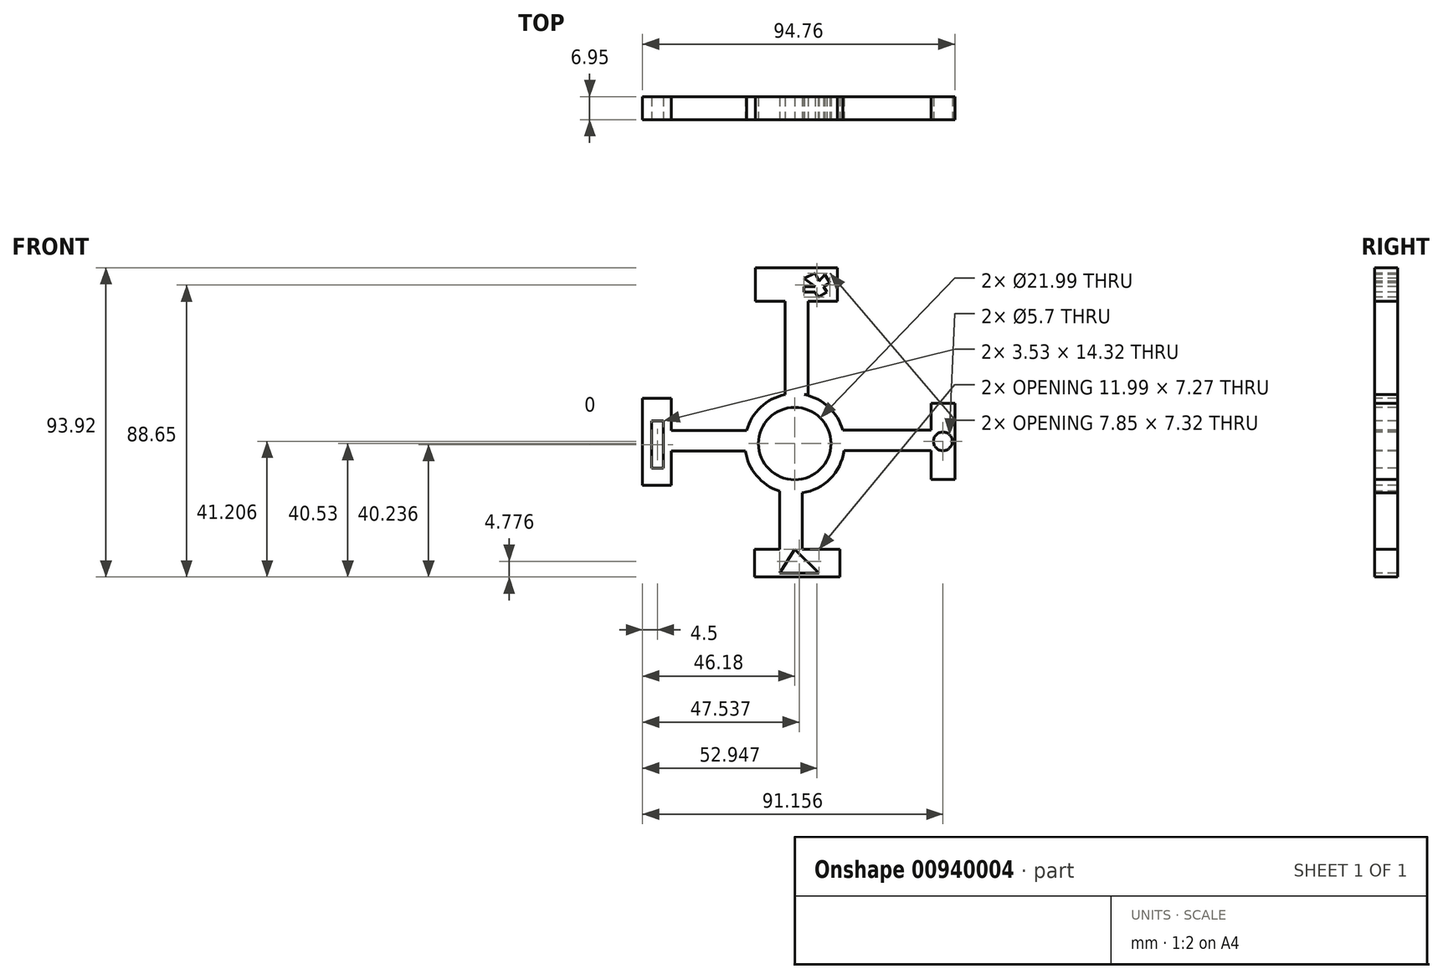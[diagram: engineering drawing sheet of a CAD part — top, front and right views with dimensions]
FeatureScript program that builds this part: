
annotation { "Feature Type Name" : "Feature", "Feature Type Description" : "" }
export const myFeature = defineFeature(function(context is Context, id is Id, definition is map)
    precondition{}
    {
        {
            var Q0;
            Q0=qCreatedBy(makeId("Front.planeOp"),FACE);
            var sketch = newSketch(context, id + "F0", { "sketchPlane" : qUnion([Q0])});
            skCircle(sketch, "E0", {"center": v(0, 0) * mm, "radius": 15.15 * mm});
            skLineSegment(sketch, "E1.bottom", {"start": v(-2.97, 14.85) * mm, "end": v(4.06, 14.85) * mm});
            skLineSegment(sketch, "E1.top", {"start": v(-2.97, 43.18) * mm, "end": v(4.06, 43.18) * mm});
            skLineSegment(sketch, "E1.left", {"start": v(-2.97, 14.85) * mm, "end": v(-2.97, 43.18) * mm});
            skLineSegment(sketch, "E1.right", {"start": v(4.06, 14.85) * mm, "end": v(4.06, 43.18) * mm});
            skLineSegment(sketch, "E2.bottom", {"start": v(-14.61, 4) * mm, "end": v(-37.47, 4) * mm});
            skLineSegment(sketch, "E2.top", {"start": v(-14.61, -2.19) * mm, "end": v(-37.47, -2.19) * mm});
            skLineSegment(sketch, "E2.left", {"start": v(-14.61, 4) * mm, "end": v(-14.61, -2.19) * mm});
            skLineSegment(sketch, "E2.right", {"start": v(-37.47, 4) * mm, "end": v(-37.47, -2.19) * mm});
            skLineSegment(sketch, "E3.bottom", {"start": v(-4.64, -14.42) * mm, "end": v(2.25, -14.42) * mm});
            skLineSegment(sketch, "E3.top", {"start": v(-4.64, -32.12) * mm, "end": v(2.25, -32.12) * mm});
            skLineSegment(sketch, "E3.left", {"start": v(-4.64, -14.42) * mm, "end": v(-4.64, -32.12) * mm});
            skLineSegment(sketch, "E3.right", {"start": v(2.25, -14.42) * mm, "end": v(2.25, -32.12) * mm});
            skLineSegment(sketch, "E4.bottom", {"start": v(14.6, 4.05) * mm, "end": v(41.37, 4.05) * mm});
            skLineSegment(sketch, "E4.top", {"start": v(14.6, -2.18) * mm, "end": v(41.37, -2.18) * mm});
            skLineSegment(sketch, "E4.left", {"start": v(14.6, 4.05) * mm, "end": v(14.6, -2.18) * mm});
            skLineSegment(sketch, "E4.right", {"start": v(41.37, 4.05) * mm, "end": v(41.37, -2.18) * mm});
            skLineSegment(sketch, "E5.bottom", {"start": v(-11.93, 43.18) * mm, "end": v(13, 43.18) * mm});
            skLineSegment(sketch, "E5.top", {"start": v(-11.93, 53.4) * mm, "end": v(13, 53.4) * mm});
            skLineSegment(sketch, "E5.left", {"start": v(-11.93, 43.18) * mm, "end": v(-11.93, 53.4) * mm});
            skLineSegment(sketch, "E5.right", {"start": v(13, 43.18) * mm, "end": v(13, 53.4) * mm});
            skLineSegment(sketch, "E6.bottom", {"start": v(41.37, 12.23) * mm, "end": v(48.58, 12.23) * mm});
            skLineSegment(sketch, "E6.top", {"start": v(41.37, -10.88) * mm, "end": v(48.58, -10.88) * mm});
            skLineSegment(sketch, "E6.left", {"start": v(41.37, 12.23) * mm, "end": v(41.37, -10.88) * mm});
            skLineSegment(sketch, "E6.right", {"start": v(48.58, 12.23) * mm, "end": v(48.58, -10.88) * mm});
            skLineSegment(sketch, "E7.bottom", {"start": v(-12.17, -32.12) * mm, "end": v(13.66, -32.12) * mm});
            skLineSegment(sketch, "E7.top", {"start": v(-12.17, -40.53) * mm, "end": v(13.66, -40.53) * mm});
            skLineSegment(sketch, "E7.left", {"start": v(-12.17, -32.12) * mm, "end": v(-12.17, -40.53) * mm});
            skLineSegment(sketch, "E7.right", {"start": v(13.66, -32.12) * mm, "end": v(13.66, -40.53) * mm});
            skLineSegment(sketch, "E8.bottom", {"start": v(-37.47, -12.7) * mm, "end": v(-46.18, -12.7) * mm});
            skLineSegment(sketch, "E8.top", {"start": v(-37.47, 13.72) * mm, "end": v(-46.18, 13.72) * mm});
            skLineSegment(sketch, "E8.left", {"start": v(-37.47, -12.7) * mm, "end": v(-37.47, 13.72) * mm});
            skLineSegment(sketch, "E8.right", {"start": v(-46.18, -12.7) * mm, "end": v(-46.18, 13.72) * mm});
            skCircle(sketch, "E9", {"center": v(44.98, 0.68) * mm, "radius": 2.85 * mm});
            skPoint(sketch, "E9.centerSnap0", {"position": v(48.58, 0.68) * mm});
            skPoint(sketch, "E9.centerSnap1", {"position": v(44.98, -10.88) * mm});
            skLineSegment(sketch, "E10", {"start": v(0, -32.12) * mm, "end": v(-4.64, -39.39) * mm});
            skLineSegment(sketch, "E11", {"start": v(-4.64, -39.39) * mm, "end": v(7.35, -39.39) * mm});
            skLineSegment(sketch, "E12", {"start": v(7.35, -39.39) * mm, "end": v(0, -32.12) * mm});
            skCircle(sketch, "E13", {"center": v(0, 0) * mm, "radius": 11 * mm});
            skPoint(sketch, "E14.endSnap0", {"position": v(0.54, 53.4) * mm});
            skLineSegment(sketch, "E15", {"start": v(9.12, 51.39) * mm, "end": v(10.69, 48.84) * mm});
            skLineSegment(sketch, "E16", {"start": v(10.69, 48.84) * mm, "end": v(8.73, 47.63) * mm});
            skLineSegment(sketch, "E17", {"start": v(8.73, 47.63) * mm, "end": v(9.71, 46.04) * mm});
            skPoint(sketch, "E17.endSnap0", {"position": v(9.71, 48.24) * mm});
            skLineSegment(sketch, "E18", {"start": v(9.71, 46.04) * mm, "end": v(7.14, 44.46) * mm});
            skLineSegment(sketch, "E19", {"start": v(7.14, 44.46) * mm, "end": v(6.16, 46.04) * mm});
            skLineSegment(sketch, "E20", {"start": v(6.16, 46.04) * mm, "end": v(2.84, 46.04) * mm});
            skLineSegment(sketch, "E21", {"start": v(2.84, 46.04) * mm, "end": v(2.84, 47.63) * mm});
            skLineSegment(sketch, "E22", {"start": v(2.84, 47.63) * mm, "end": v(6.18, 47.63) * mm});
            skLineSegment(sketch, "E23", {"start": v(6.18, 47.63) * mm, "end": v(2.84, 50.21) * mm});
            skLineSegment(sketch, "E24", {"start": v(2.84, 50.21) * mm, "end": v(6.18, 51.78) * mm});
            skLineSegment(sketch, "E25", {"start": v(6.18, 51.78) * mm, "end": v(7.33, 49.32) * mm});
            skLineSegment(sketch, "E26", {"start": v(9.12, 51.39) * mm, "end": v(7.33, 49.32) * mm});
            skLineSegment(sketch, "E27.bottom", {"start": v(-43.44, 6.86) * mm, "end": v(-39.91, 6.86) * mm});
            skLineSegment(sketch, "E27.top", {"start": v(-43.44, -7.45) * mm, "end": v(-39.91, -7.45) * mm});
            skLineSegment(sketch, "E27.left", {"start": v(-43.44, 6.86) * mm, "end": v(-43.44, -7.45) * mm});
            skLineSegment(sketch, "E27.right", {"start": v(-39.91, 6.86) * mm, "end": v(-39.91, -7.45) * mm});
            skSolve(sketch);
        }
        {
            var Q0;
            Q0 = qSketchRegion(id + "F0", true);
            extrude(context, id + "F1", {"entities" : qUnion([Q0]), "oppositeDirection" : true, "depth" : 6.95 * mm, "offsetDistance" : 25 * mm});
        }
    });
